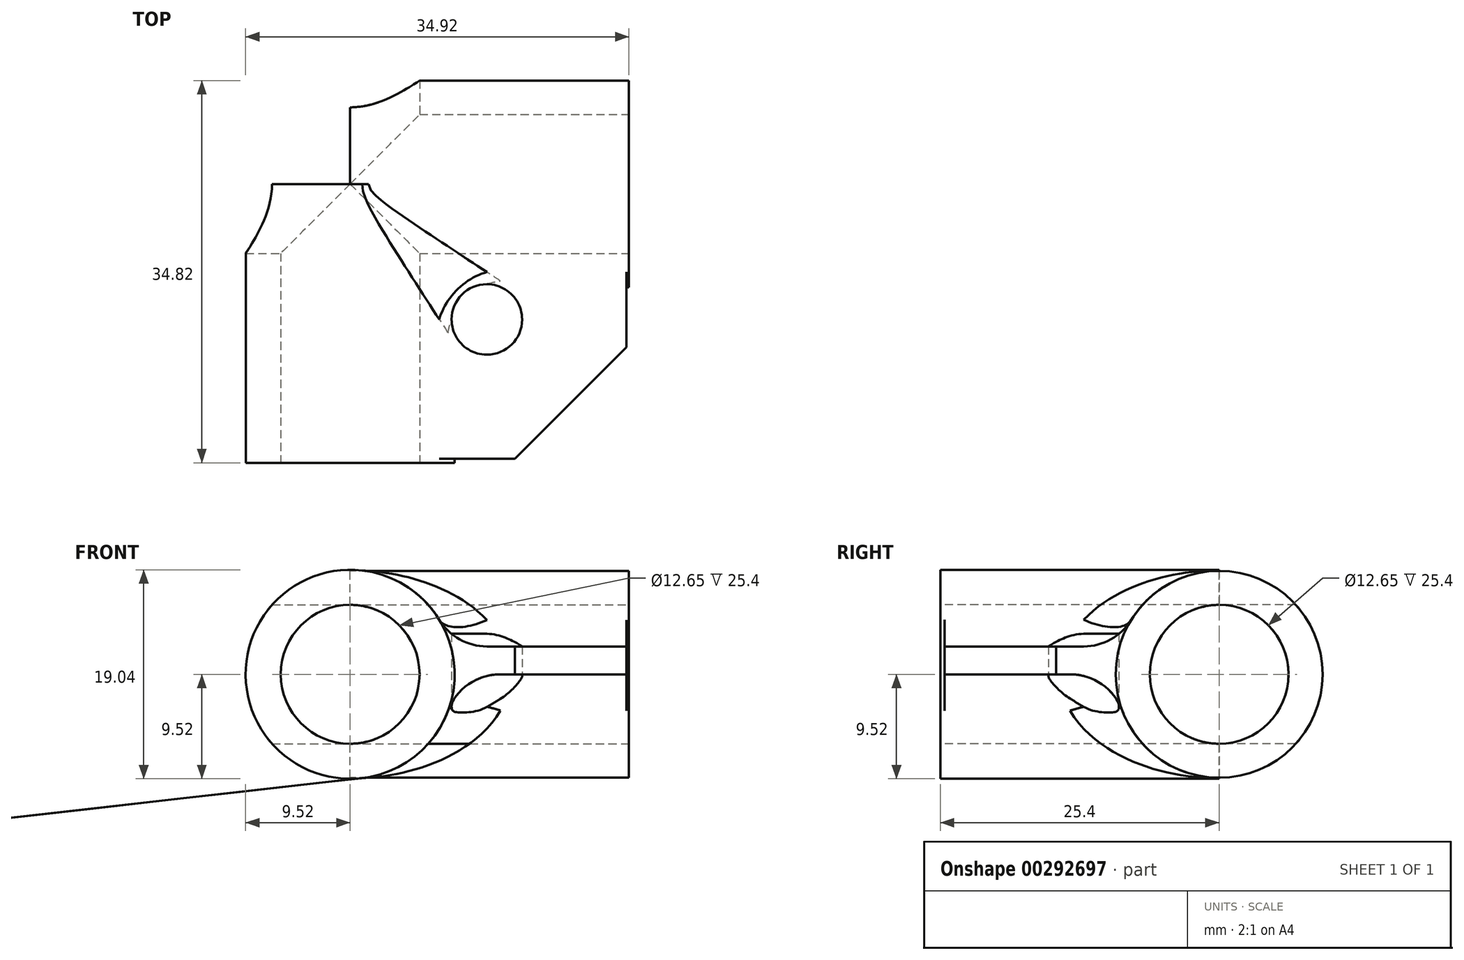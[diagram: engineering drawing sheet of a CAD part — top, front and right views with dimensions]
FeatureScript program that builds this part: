
annotation { "Feature Type Name" : "Feature", "Feature Type Description" : "" }
export const myFeature = defineFeature(function(context is Context, id is Id, definition is map)
    precondition{}
    {
        {
            var Q0;
            Q0=qCreatedBy(makeId("Front.planeOp"),FACE);
            var sketch = newSketch(context, id + "F0", { "sketchPlane" : qUnion([Q0])});
            skCircle(sketch, "E0", {"center": v(0, 0) * mm, "radius": 9.52 * mm});
            skSolve(sketch);
        }
        {
            var Q0;
            Q0=makeQuery(id+"F0.imprint","IMPRINT",FACE,{"disambiguationData":[TD([[makeQuery(id+"F0.imprint","IMPRINT",EDGE,{"derivedFrom":sQuery(id+"F0.wireOp",EDGE,"E0")}),1.0]])]});
            extrude(context, id + "F1", {"entities" : qUnion([Q0]), "depth" : 25.4 * mm});
        }
        {
            var Q0;
            Q0=qCreatedBy(makeId("Right.planeOp"),FACE);
            var sketch = newSketch(context, id + "F2", { "sketchPlane" : qUnion([Q0])});
            skCircle(sketch, "E1", {"center": v(0, 0) * mm, "radius": 9.42 * mm});
            skSolve(sketch);
        }
        {
            var Q0;
            Q0=makeQuery(id+"F2.imprint","IMPRINT",FACE,{"disambiguationData":[TD([[makeQuery(id+"F2.imprint","IMPRINT",EDGE,{"derivedFrom":sQuery(id+"F2.wireOp",EDGE,"E1")}),1.0]])]});
            extrude(context, id + "F3", {"entities" : qUnion([Q0]), "operationType" : NewBodyOperationType.ADD, "depth" : 25.4 * mm});
        }
        {
            var Q0;
            Q0=qCreatedBy(makeId("Top.planeOp"),FACE);
            var sketch = newSketch(context, id + "F4", { "sketchPlane" : qUnion([Q0])});
            skLineSegment(sketch, "E2.bottom", {"start": v(0, 0) * mm, "end": v(25.16, 0) * mm});
            skLineSegment(sketch, "E2.top", {"start": v(0, -25.03) * mm, "end": v(25.16, -25.03) * mm});
            skLineSegment(sketch, "E2.left", {"start": v(0, 0) * mm, "end": v(0, -25.03) * mm});
            skLineSegment(sketch, "E2.right", {"start": v(25.16, 0) * mm, "end": v(25.16, -25.03) * mm});
            skSolve(sketch);
        }
        {
            var Q0;
            Q0=makeQuery(id+"F4.imprint","IMPRINT",FACE,{"disambiguationData":[TD([[makeQuery(id+"F4.imprint","IMPRINT",EDGE,{"derivedFrom":sQuery(id+"F4.wireOp",EDGE,"E2.bottom")}),-1.0]])]});
            extrude(context, id + "F5", {"entities" : qUnion([Q0]), "operationType" : NewBodyOperationType.ADD, "depth" : 2.54 * mm});
        }
        {
            var Q0;
            Q0=makeQuery(id+"F5.boolean.opBoolean","INTERSECT",EDGE,{"derivedFrom":[makeQuery(id+"F1.opExtrude","SWEPT_FACE",FACE,{"disambiguationData":[OSD([sQuery(id+"F0.wireOp",EDGE,"E0")])]}),makeQuery(id+"F5.opExtrude","CAP_FACE",FACE,{"disambiguationData":[OSD([sQuery(id+"F4.wireOp",EDGE,"E2.bottom"),sQuery(id+"F4.wireOp",EDGE,"E2.top"),sQuery(id+"F4.wireOp",EDGE,"E2.left"),sQuery(id+"F4.wireOp",EDGE,"E2.right")])],"isStart":false})]});
            var Q1;
            Q1=makeQuery(id+"F5.boolean.opBoolean","INTERSECT",EDGE,{"derivedFrom":[makeQuery(id+"F3.opExtrude","SWEPT_FACE",FACE,{"disambiguationData":[OSD([sQuery(id+"F2.wireOp",EDGE,"E1")])]}),makeQuery(id+"F5.opExtrude","CAP_FACE",FACE,{"disambiguationData":[OSD([sQuery(id+"F4.wireOp",EDGE,"E2.bottom"),sQuery(id+"F4.wireOp",EDGE,"E2.top"),sQuery(id+"F4.wireOp",EDGE,"E2.left"),sQuery(id+"F4.wireOp",EDGE,"E2.right")])],"isStart":false})]});
            var Q2;
            {var subQ0=sQuery(id+"F0.wireOp",EDGE,"E0");var subQ1=makeQuery(id+"F1.opExtrude","SWEPT_FACE",FACE,{"disambiguationData":[OSD([subQ0])]});var subQ2=makeQuery(id+"F3.opExtrude","SWEPT_FACE",FACE,{"disambiguationData":[OSD([sQuery(id+"F2.wireOp",EDGE,"E1")])]});Q2=makeQuery(id+"F5.boolean.opBoolean","SPLIT",EDGE,{"disambiguationData":[TD([makeQuery(id+"F5.opExtrude","CAP_FACE",FACE,{"disambiguationData":[OSD([sQuery(id+"F4.wireOp",EDGE,"E2.bottom"),sQuery(id+"F4.wireOp",EDGE,"E2.top"),sQuery(id+"F4.wireOp",EDGE,"E2.left"),sQuery(id+"F4.wireOp",EDGE,"E2.right")])],"isStart":false})])],"derivedFrom":makeQuery(id+"F3.boolean.opBoolean","INTERSECT",EDGE,{"derivedFrom":[subQ1,subQ2]})});}
            fillet(context, id + "F6", {"entities" : qUnion([Q0, Q1, Q2]), "radius" : 5.08 * mm, "tangentPropagation" : true, "allowEdgeOverflow" : false});
        }
        {
            var Q0;
            Q0=makeQuery(id+"F5.boolean.opBoolean","INTERSECT",EDGE,{"derivedFrom":[makeQuery(id+"F1.opExtrude","SWEPT_FACE",FACE,{"disambiguationData":[OSD([sQuery(id+"F0.wireOp",EDGE,"E0")])]}),makeQuery(id+"F5.opExtrude","CAP_FACE",FACE,{"disambiguationData":[OSD([sQuery(id+"F4.wireOp",EDGE,"E2.bottom"),sQuery(id+"F4.wireOp",EDGE,"E2.top"),sQuery(id+"F4.wireOp",EDGE,"E2.left"),sQuery(id+"F4.wireOp",EDGE,"E2.right")])],"isStart":true})]});
            var Q1;
            Q1=makeQuery(id+"F5.boolean.opBoolean","INTERSECT",EDGE,{"derivedFrom":[makeQuery(id+"F3.opExtrude","SWEPT_FACE",FACE,{"disambiguationData":[OSD([sQuery(id+"F2.wireOp",EDGE,"E1")])]}),makeQuery(id+"F5.opExtrude","CAP_FACE",FACE,{"disambiguationData":[OSD([sQuery(id+"F4.wireOp",EDGE,"E2.bottom"),sQuery(id+"F4.wireOp",EDGE,"E2.top"),sQuery(id+"F4.wireOp",EDGE,"E2.left"),sQuery(id+"F4.wireOp",EDGE,"E2.right")])],"isStart":true})]});
            var Q2;
            {var subQ0=sQuery(id+"F0.wireOp",EDGE,"E0");var subQ1=makeQuery(id+"F1.opExtrude","SWEPT_FACE",FACE,{"disambiguationData":[OSD([subQ0])]});var subQ2=makeQuery(id+"F3.opExtrude","SWEPT_FACE",FACE,{"disambiguationData":[OSD([sQuery(id+"F2.wireOp",EDGE,"E1")])]});Q2=makeQuery(id+"F5.boolean.opBoolean","SPLIT",EDGE,{"disambiguationData":[TD([makeQuery(id+"F5.opExtrude","CAP_FACE",FACE,{"disambiguationData":[OSD([sQuery(id+"F4.wireOp",EDGE,"E2.bottom"),sQuery(id+"F4.wireOp",EDGE,"E2.top"),sQuery(id+"F4.wireOp",EDGE,"E2.left"),sQuery(id+"F4.wireOp",EDGE,"E2.right")])],"isStart":true})])],"derivedFrom":makeQuery(id+"F3.boolean.opBoolean","INTERSECT",EDGE,{"derivedFrom":[subQ1,subQ2]})});}
            fillet(context, id + "F7", {"entities" : qUnion([Q0, Q1, Q2]), "radius" : 5.08 * mm, "tangentPropagation" : true, "allowEdgeOverflow" : false});
        }
        {
            var Q0;
            Q0=makeQuery(id+"F3.opExtrude","CAP_FACE",FACE,{"disambiguationData":[OSD([sQuery(id+"F2.wireOp",EDGE,"E1")])],"isStart":false});
            var sketch = newSketch(context, id + "F8", { "sketchPlane" : qUnion([Q0])});
            skPoint(sketch, "E3", {"position": v(0, 0) * mm});
            skSolve(sketch);
        }
        {
            var Q0;
            Q0=sQuery(id+"F8.wireOp",VERTEX,"E3");
            var Q1;
            Q1=makeQuery(id+"F1.opExtrude","SWEPT_BODY",BODY,{"disambiguationData":[OSD([sQuery(id+"F0.wireOp",EDGE,"E0")])]});
            hole(context, id + "F9", {"style" : HoleStyle.SIMPLE, "endStyle" : HoleEndStyle.THROUGH, "holeDiameter" : 12.65 * mm, "tappedDepth" : 12.7 * mm, "tapClearance" : 3, "locations" : qUnion([Q0]), "scope" : qUnion([Q1])});
        }
        {
            var Q0;
            Q0=makeQuery(id+"F1.opExtrude","CAP_FACE",FACE,{"disambiguationData":[OSD([sQuery(id+"F0.wireOp",EDGE,"E0")])],"isStart":false});
            var sketch = newSketch(context, id + "F10", { "sketchPlane" : qUnion([Q0])});
            skPoint(sketch, "E4", {"position": v(0, 0) * mm});
            skSolve(sketch);
        }
        {
            var Q0;
            Q0=sQuery(id+"F10.wireOp",VERTEX,"E4");
            var Q1;
            Q1=makeQuery(id+"F1.opExtrude","SWEPT_BODY",BODY,{"disambiguationData":[OSD([sQuery(id+"F0.wireOp",EDGE,"E0")])]});
            hole(context, id + "F11", {"style" : HoleStyle.SIMPLE, "endStyle" : HoleEndStyle.THROUGH, "holeDiameter" : 12.65 * mm, "tappedDepth" : 12.7 * mm, "tapClearance" : 3, "locations" : qUnion([Q0]), "scope" : qUnion([Q1])});
        }
        {
            var Q0;
            Q0=makeQuery(id+"F5.opExtrude","SWEPT_EDGE",EDGE,{"disambiguationData":[OSD([sQuery(id+"F4.wireOp",EDGE,"E2.top"),sQuery(id+"F4.wireOp",EDGE,"E2.right")])]});
            chamfer(context, id + "F12", {"entities" : qUnion([Q0]), "width" : 10.16 * mm, "tangentPropagation" : true});
        }
        {
            var Q0;
            Q0=makeQuery(id+"F5.opExtrude","CAP_FACE",FACE,{"disambiguationData":[OSD([sQuery(id+"F4.wireOp",EDGE,"E2.bottom"),sQuery(id+"F4.wireOp",EDGE,"E2.top"),sQuery(id+"F4.wireOp",EDGE,"E2.left"),sQuery(id+"F4.wireOp",EDGE,"E2.right")])],"isStart":false});
            var sketch = newSketch(context, id + "F13", { "sketchPlane" : qUnion([Q0])});
            skPoint(sketch, "E5", {"position": v(12.45, -12.34) * mm});
            skSolve(sketch);
        }
        {
            var Q0;
            Q0=sQuery(id+"F13.wireOp",VERTEX,"E5");
            var Q1;
            Q1=makeQuery(id+"F1.opExtrude","SWEPT_BODY",BODY,{"disambiguationData":[OSD([sQuery(id+"F0.wireOp",EDGE,"E0")])]});
            hole(context, id + "F14", {"style" : HoleStyle.SIMPLE, "endStyle" : HoleEndStyle.THROUGH, "oppositeDirection" : true, "holeDiameter" : 6.43 * mm, "tappedDepth" : 12.7 * mm, "tapClearance" : 3, "locations" : qUnion([Q0]), "scope" : qUnion([Q1])});
        }
        {
            var Q0;
            Q0=sQuery(id+"F13.wireOp",VERTEX,"E5");
            var Q1;
            Q1=makeQuery(id+"F1.opExtrude","SWEPT_BODY",BODY,{"disambiguationData":[OSD([sQuery(id+"F0.wireOp",EDGE,"E0")])]});
            hole(context, id + "F15", {"style" : HoleStyle.SIMPLE, "endStyle" : HoleEndStyle.THROUGH, "holeDiameter" : 6.43 * mm, "tappedDepth" : 12.7 * mm, "tapClearance" : 3, "locations" : qUnion([Q0]), "scope" : qUnion([Q1])});
        }
    });
